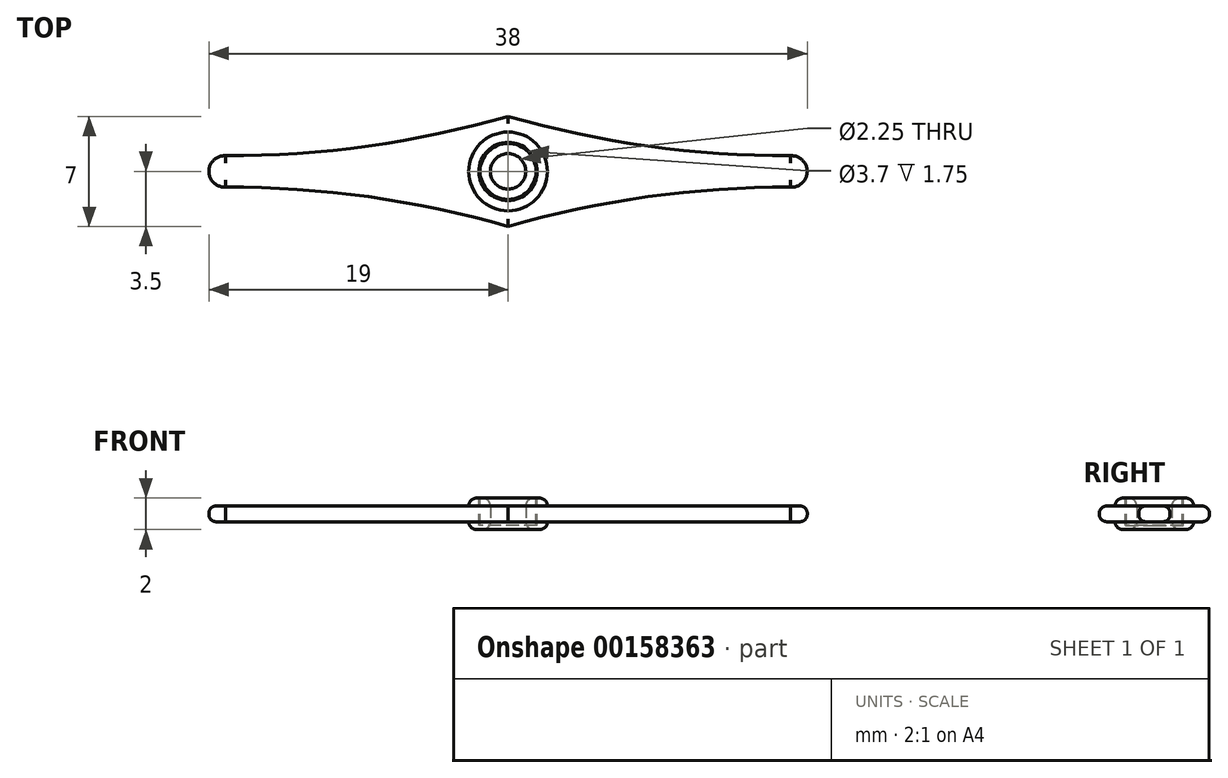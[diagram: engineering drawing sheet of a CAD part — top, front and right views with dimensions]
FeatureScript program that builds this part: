
annotation { "Feature Type Name" : "Feature", "Feature Type Description" : "" }
export const myFeature = defineFeature(function(context is Context, id is Id, definition is map)
    precondition{}
    {
        {
            var Q0;
            Q0=qCreatedBy(makeId("Top.planeOp"),FACE);
            var sketch = newSketch(context, id + "F0", { "sketchPlane" : qUnion([Q0])});
            skCircle(sketch, "E0", {"center": v(0, 0) * mm, "radius": 1.13 * mm});
            skCircle(sketch, "E1", {"center": v(0, 0) * mm, "radius": 2.5 * mm});
            skSolve(sketch);
        }
        {
            var Q0;
            Q0=makeQuery(id+"F0.imprint","IMPRINT",FACE,{"disambiguationData":[TD([[makeQuery(id+"F0.imprint","IMPRINT",EDGE,{"derivedFrom":sQuery(id+"F0.wireOp",EDGE,"E0")}),-1.0]])]});
            extrude(context, id + "F1", {"entities" : qUnion([Q0]), "endBound" : BoundingType.SYMMETRIC, "depth" : 2 * mm});
        }
        {
            var Q0;
            Q0=makeQuery(id+"F1.opExtrude","CAP_EDGE",EDGE,{"disambiguationData":[OSD([sQuery(id+"F0.wireOp",EDGE,"E1")])],"isStart":false});
            var Q1;
            Q1=makeQuery(id+"F1.opExtrude","CAP_EDGE",EDGE,{"disambiguationData":[OSD([sQuery(id+"F0.wireOp",EDGE,"E0")])],"isStart":false});
            var Q2;
            Q2=makeQuery(id+"F1.opExtrude","CAP_EDGE",EDGE,{"disambiguationData":[OSD([sQuery(id+"F0.wireOp",EDGE,"E1")])],"isStart":true});
            var Q3;
            Q3=makeQuery(id+"F1.opExtrude","CAP_EDGE",EDGE,{"disambiguationData":[OSD([sQuery(id+"F0.wireOp",EDGE,"E0")])],"isStart":true});
            fillet(context, id + "F2", {"entities" : qUnion([Q0, Q1, Q2, Q3]), "radius" : .5 * mm, "tangentPropagation" : true, "allowEdgeOverflow" : false});
        }
        {
            var Q0;
            Q0=makeQuery(id+"F1.opExtrude","CAP_FACE",FACE,{"disambiguationData":[OSD([sQuery(id+"F0.wireOp",EDGE,"E0"),sQuery(id+"F0.wireOp",EDGE,"E1")])],"isStart":false});
            var sketch = newSketch(context, id + "F3", { "sketchPlane" : qUnion([Q0])});
            skCircle(sketch, "E2.0", {"center": v(0, 0) * mm, "radius": 1.63 * mm});
            skCircle(sketch, "E3.0", {"center": v(0, 0) * mm, "radius": 2 * mm});
            skCircle(sketch, "E4", {"center": v(0, 0) * mm, "radius": 1.78 * mm});
            skCircle(sketch, "E5", {"center": v(0, 0) * mm, "radius": 1.85 * mm});
            skSolve(sketch);
        }
        {
            var Q0;
            Q0=makeQuery(id+"F3.imprint","IMPRINT",FACE,{"disambiguationData":[TD([[makeQuery(id+"F3.imprint","IMPRINT",EDGE,{"derivedFrom":sQuery(id+"F3.wireOp",EDGE,"E4")}),-1.0]])]});
            extrude(context, id + "F4", {"entities" : qUnion([Q0]), "operationType" : NewBodyOperationType.REMOVE, "oppositeDirection" : true, "depth" : 1.75 * mm});
        }
        {
            var Q0;
            Q0=makeQuery(id+"F4.boolean.opBoolean","COPY",EDGE,{"derivedFrom":makeQuery(id+"F4.opExtrude","CAP_EDGE",EDGE,{"disambiguationData":[OSD([sQuery(id+"F3.wireOp",EDGE,"E5")])],"isStart":true})});
            var Q1;
            Q1=makeQuery(id+"F4.boolean.opBoolean","COPY",EDGE,{"derivedFrom":makeQuery(id+"F4.opExtrude","CAP_EDGE",EDGE,{"disambiguationData":[OSD([sQuery(id+"F3.wireOp",EDGE,"E4")])],"isStart":true})});
            var Q2;
            Q2=makeQuery(id+"F4.boolean.opBoolean","INTERSECT",EDGE,{"derivedFrom":[makeQuery(id+"F1.opExtrude","CAP_FACE",FACE,{"disambiguationData":[OSD([sQuery(id+"F0.wireOp",EDGE,"E0"),sQuery(id+"F0.wireOp",EDGE,"E1")])],"isStart":true}),makeQuery(id+"F4.opExtrude","SWEPT_FACE",FACE,{"disambiguationData":[OSD([sQuery(id+"F3.wireOp",EDGE,"E4")])]})]});
            var Q3;
            Q3=makeQuery(id+"F4.boolean.opBoolean","INTERSECT",EDGE,{"derivedFrom":[makeQuery(id+"F1.opExtrude","CAP_FACE",FACE,{"disambiguationData":[OSD([sQuery(id+"F0.wireOp",EDGE,"E0"),sQuery(id+"F0.wireOp",EDGE,"E1")])],"isStart":true}),makeQuery(id+"F4.opExtrude","SWEPT_FACE",FACE,{"disambiguationData":[OSD([sQuery(id+"F3.wireOp",EDGE,"E5")])]})]});
            fillet(context, id + "F5", {"entities" : qUnion([Q0, Q1, Q2, Q3]), "radius" : .1 * mm, "tangentPropagation" : true, "allowEdgeOverflow" : false});
        }
        {
            var Q0;
            Q0=qCreatedBy(makeId("Top.planeOp"),FACE);
            var sketch = newSketch(context, id + "F6", { "sketchPlane" : qUnion([Q0])});
            skCircle(sketch, "E6.0", {"center": v(0, 0) * mm, "radius": 2 * mm});
            skCircle(sketch, "E7.0", {"center": v(0, 0) * mm, "radius": 1.63 * mm});
            skLineSegment(sketch, "E8", {"start": v(0, 0) * mm, "end": v(2, 0) * mm});
            skArc(sketch, "E9", {"start": v(1.63, 0) * mm, "mid": v(1.81, -0.19) * mm, "end": v(2, 0) * mm});
            skSolve(sketch);
        }
        {
            var Q0;
            Q0=qCreatedBy(makeId("Top.planeOp"),FACE);
            var sketch = newSketch(context, id + "F7", { "sketchPlane" : qUnion([Q0])});
            skCircle(sketch, "E10", {"center": v(-18, 0) * mm, "radius": 1 * mm});
            skArc(sketch, "E11", {"start": v(0, -3.5) * mm, "mid": v(-8.94, -1.6) * mm, "end": v(-18.06, -1) * mm});
            skLineSegment(sketch, "E12", {"start": v(-18.06, -1) * mm, "end": v(0, -0.9) * mm, "construction": true});
            skCircle(sketch, "E13.0", {"center": v(0, 0) * mm, "radius": 2.5 * mm});
            skLineSegment(sketch, "E14", {"start": v(0, -3.5) * mm, "end": v(0, -2.5) * mm});
            skArc(sketch, "E15", {"start": v(-2.5, 0) * mm, "mid": v(-1.77, -1.77) * mm, "end": v(0, -2.5) * mm});
            skArc(sketch, "E16.MirrorCS", {"start": v(0, 3.5) * mm, "mid": v(-8.94, 1.6) * mm, "end": v(-18.06, 1) * mm});
            skLineSegment(sketch, "E17.MirrorCS", {"start": v(0, 3.5) * mm, "end": v(0, 2.5) * mm});
            skSolve(sketch);
        }
        {
            var Q0;
            {var subQ0=sQuery(id+"F7.wireOp",EDGE,"E16.MirrorCS");var subQ1=sQuery(id+"F7.wireOp",EDGE,"E10");var subQ2=makeQuery(id+"F7.imprint","INTERSECT",VERTEX,{"disambiguationData":[OD(0.0)],"derivedFrom":[subQ1,subQ0]});Q0=makeQuery(id+"F7.imprint","IMPRINT",FACE,{"disambiguationData":[TD([[makeQuery(id+"F7.imprint","IMPRINT",EDGE,{"disambiguationData":[TD([[subQ2,1.0]])],"derivedFrom":subQ1}),1.0]])]});}
            var Q1;
            {var subQ0=sQuery(id+"F7.wireOp",EDGE,"E11");var subQ1=sQuery(id+"F7.wireOp",EDGE,"E10");var subQ2=makeQuery(id+"F7.imprint","INTERSECT",VERTEX,{"disambiguationData":[OD(0.0)],"derivedFrom":[subQ1,subQ0]});Q1=makeQuery(id+"F7.imprint","IMPRINT",FACE,{"disambiguationData":[TD([[makeQuery(id+"F7.imprint","IMPRINT",EDGE,{"disambiguationData":[TD([[subQ2,-1.0]])],"derivedFrom":subQ1}),1.0]])]});}
            var Q2;
            {var subQ0=sQuery(id+"F7.wireOp",EDGE,"E14");Q2=makeQuery(id+"F7.imprint","IMPRINT",FACE,{"disambiguationData":[TD([[makeQuery(id+"F7.imprint","IMPRINT",EDGE,{"derivedFrom":subQ0}),1.0]])]});}
            var Q3;
            {var subQ0=sQuery(id+"F7.wireOp",EDGE,"E11");var subQ1=sQuery(id+"F7.wireOp",EDGE,"E10");var subQ2=makeQuery(id+"F7.imprint","INTERSECT",VERTEX,{"disambiguationData":[OD(0.0)],"derivedFrom":[subQ1,subQ0]});Q3=makeQuery(id+"F7.imprint","IMPRINT",FACE,{"disambiguationData":[TD([[makeQuery(id+"F7.imprint","IMPRINT",EDGE,{"disambiguationData":[TD([[subQ2,1.0]])],"derivedFrom":subQ1}),1.0]])]});}
            extrude(context, id + "F8", {"entities" : qUnion([Q0, Q1, Q2, Q3]), "endBound" : BoundingType.SYMMETRIC, "depth" : 1 * mm});
        }
        {
            var Q0;
            Q0=makeQuery(id+"F8.opExtrude","CAP_EDGE",EDGE,{"disambiguationData":[OSD([sQuery(id+"F7.wireOp",EDGE,"E16.MirrorCS")])],"isStart":true});
            var Q1;
            Q1=makeQuery(id+"F8.opExtrude","CAP_EDGE",EDGE,{"disambiguationData":[OSD([sQuery(id+"F7.wireOp",EDGE,"E10")])],"isStart":true});
            var Q2;
            Q2=makeQuery(id+"F8.opExtrude","CAP_EDGE",EDGE,{"disambiguationData":[OSD([sQuery(id+"F7.wireOp",EDGE,"E11")])],"isStart":true});
            var Q3;
            Q3=makeQuery(id+"F8.opExtrude","CAP_EDGE",EDGE,{"disambiguationData":[OSD([sQuery(id+"F7.wireOp",EDGE,"E16.MirrorCS")])],"isStart":false});
            var Q4;
            Q4=makeQuery(id+"F8.opExtrude","CAP_EDGE",EDGE,{"disambiguationData":[OSD([sQuery(id+"F7.wireOp",EDGE,"E10")])],"isStart":false});
            var Q5;
            Q5=makeQuery(id+"F8.opExtrude","CAP_EDGE",EDGE,{"disambiguationData":[OSD([sQuery(id+"F7.wireOp",EDGE,"E11")])],"isStart":false});
            fillet(context, id + "F9", {"entities" : qUnion([Q0, Q1, Q2, Q3, Q4, Q5]), "radius" : .45 * mm, "tangentPropagation" : true, "allowEdgeOverflow" : false});
        }
        {
            var Q0;
            Q0=makeQuery(id+"F8.opExtrude","SWEPT_BODY",BODY,{"disambiguationData":[OSD([sQuery(id+"F7.wireOp",EDGE,"E10"),sQuery(id+"F7.wireOp",EDGE,"E11"),sQuery(id+"F7.wireOp",EDGE,"E13.0"),sQuery(id+"F7.wireOp",EDGE,"E14"),sQuery(id+"F7.wireOp",EDGE,"E16.MirrorCS"),sQuery(id+"F7.wireOp",EDGE,"E17.MirrorCS")])]});
            var Q1;
            Q1=makeQuery(id+"F8.opExtrude","SWEPT_FACE",FACE,{"disambiguationData":[OSD([sQuery(id+"F7.wireOp",EDGE,"E14")])]});
            mirror(context, id + "F10", {"operationType" : NewBodyOperationType.ADD, "entities" : qUnion([Q0]), "mirrorPlane" : qUnion([Q1])});
        }
    });
